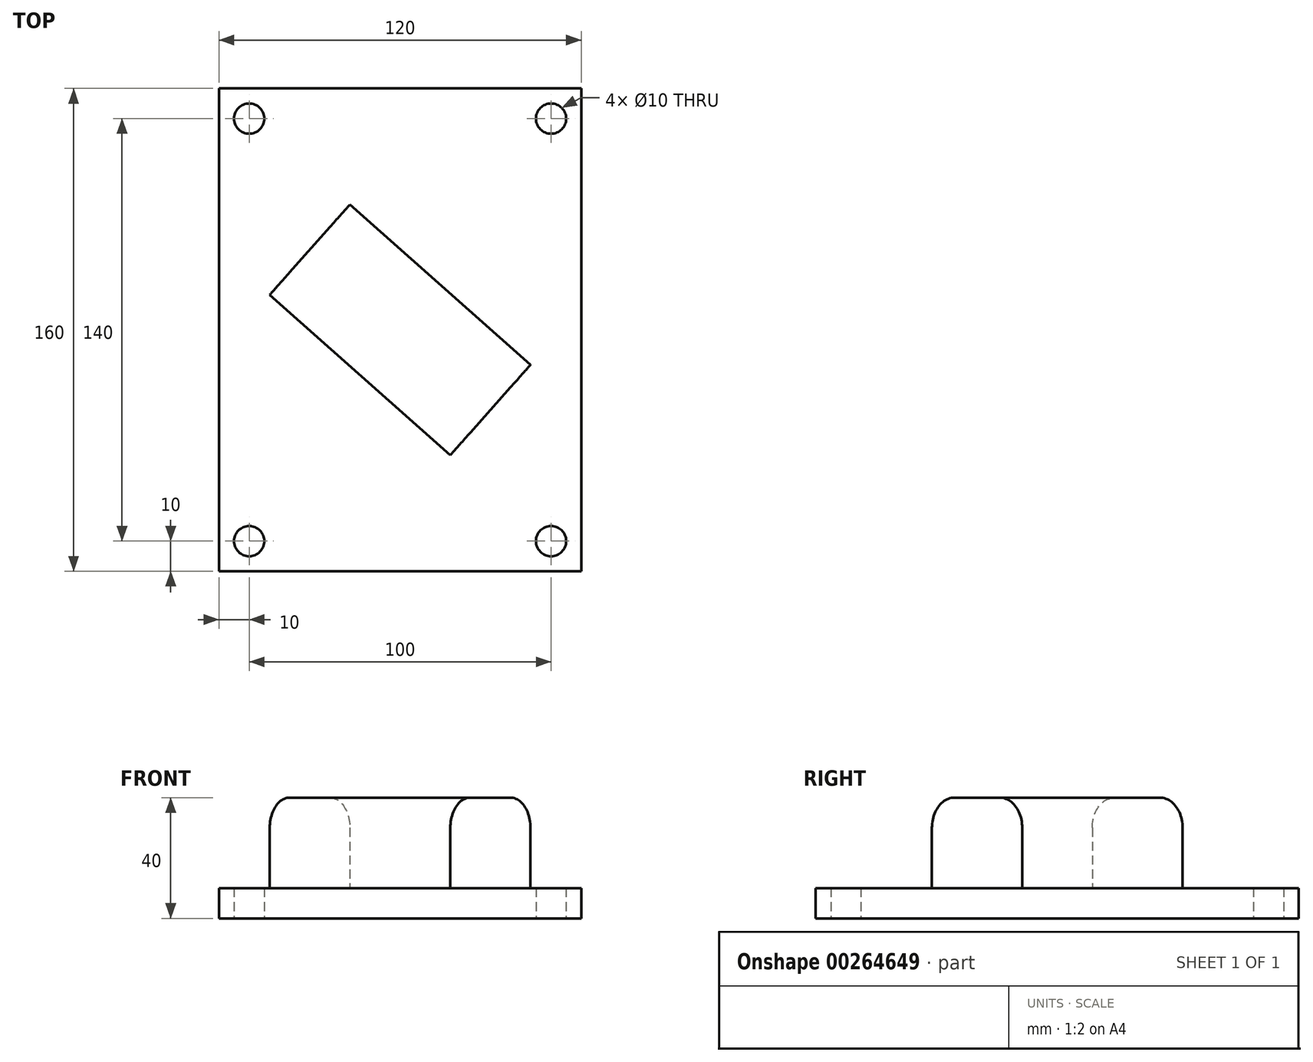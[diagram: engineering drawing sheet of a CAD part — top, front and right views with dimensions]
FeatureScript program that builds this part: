
annotation { "Feature Type Name" : "Feature", "Feature Type Description" : "" }
export const myFeature = defineFeature(function(context is Context, id is Id, definition is map)
    precondition{}
    {
        {
            var Q0;
            Q0=qCreatedBy(makeId("Top.planeOp"),FACE);
            var sketch = newSketch(context, id + "F0", { "sketchPlane" : qUnion([Q0])});
            skLineSegment(sketch, "E0.bottom", {"start": v(-60, 80) * mm, "end": v(60, 80) * mm});
            skLineSegment(sketch, "E0.top", {"start": v(-60, -80) * mm, "end": v(60, -80) * mm});
            skLineSegment(sketch, "E0.left", {"start": v(-60, 80) * mm, "end": v(-60, -80) * mm});
            skLineSegment(sketch, "E0.right", {"start": v(60, 80) * mm, "end": v(60, -80) * mm});
            skPoint(sketch, "E0.middle", {"position": v(0, 0) * mm});
            skLineSegment(sketch, "E1.0", {"start": v(-50, 70) * mm, "end": v(50, 70) * mm, "construction": true});
            skLineSegment(sketch, "E1.1", {"start": v(-50, 70) * mm, "end": v(-50, -70) * mm, "construction": true});
            skLineSegment(sketch, "E1.2", {"start": v(-50, -70) * mm, "end": v(50, -70) * mm, "construction": true});
            skLineSegment(sketch, "E1.3", {"start": v(50, 70) * mm, "end": v(50, -70) * mm, "construction": true});
            skCircle(sketch, "E2", {"center": v(-50, 70) * mm, "radius": 5 * mm});
            skCircle(sketch, "E3", {"center": v(-50, -70) * mm, "radius": 5 * mm});
            skCircle(sketch, "E4", {"center": v(50, -70) * mm, "radius": 5 * mm});
            skCircle(sketch, "E5", {"center": v(50, 70) * mm, "radius": 5 * mm});
            skLineSegment(sketch, "E6", {"start": v(43.2, -11.6) * mm, "end": v(16.64, -41.51) * mm});
            skLineSegment(sketch, "E7", {"start": v(-43.2, 11.6) * mm, "end": v(-16.64, 41.51) * mm});
            skLineSegment(sketch, "E8", {"start": v(-16.64, 41.51) * mm, "end": v(43.2, -11.6) * mm});
            skLineSegment(sketch, "E9", {"start": v(-16.64, 41.51) * mm, "end": v(-60, 80) * mm, "construction": true});
            skLineSegment(sketch, "E10", {"start": v(-43.2, 11.6) * mm, "end": v(16.64, -41.51) * mm});
            skLineSegment(sketch, "E11", {"start": v(16.64, -41.51) * mm, "end": v(60, -80) * mm, "construction": true});
            skSolve(sketch);
        }
        {
            var Q0;
            Q0=makeQuery(id+"F0.imprint","IMPRINT",FACE,{"disambiguationData":[TD([[makeQuery(id+"F0.imprint","IMPRINT",EDGE,{"derivedFrom":sQuery(id+"F0.wireOp",EDGE,"E6")}),-1.0]])]});
            extrude(context, id + "F1", {"entities" : qUnion([Q0]), "depth" : 40 * mm, "offsetDistance" : 25 * mm});
        }
        {
            var Q0;
            Q0=makeQuery(id+"F0.imprint","IMPRINT",FACE,{"disambiguationData":[TD([[makeQuery(id+"F0.imprint","IMPRINT",EDGE,{"derivedFrom":sQuery(id+"F0.wireOp",EDGE,"E0.bottom")}),-1.0]])]});
            extrude(context, id + "F2", {"entities" : qUnion([Q0]), "operationType" : NewBodyOperationType.ADD, "depth" : 10 * mm, "offsetDistance" : 25 * mm});
        }
        {
            var Q0;
            Q0=makeQuery(id+"F1.opExtrude","CAP_EDGE",EDGE,{"disambiguationData":[OSD([sQuery(id+"F0.wireOp",EDGE,"E8")])],"isStart":false});
            var Q1;
            Q1=makeQuery(id+"F1.opExtrude","CAP_EDGE",EDGE,{"disambiguationData":[OSD([sQuery(id+"F0.wireOp",EDGE,"E10")])],"isStart":false});
            fillet(context, id + "F3", {"entities" : qUnion([Q0, Q1]), "radius" : 10 * mm, "tangentPropagation" : true, "allowEdgeOverflow" : false});
        }
    });
